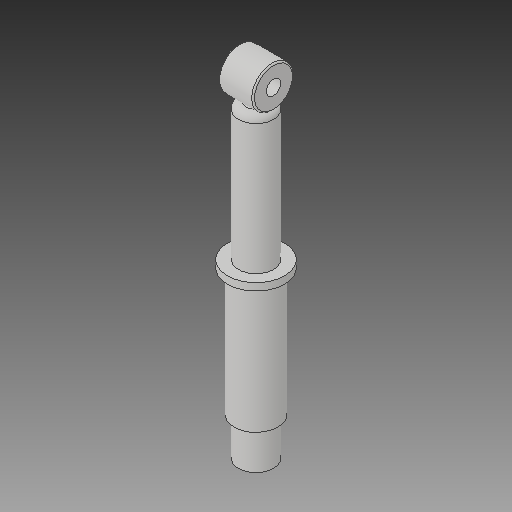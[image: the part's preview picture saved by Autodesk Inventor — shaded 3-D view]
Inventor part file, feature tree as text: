
AUTODESK INVENTOR PART (.ipt)
format: ipt  version: 2018 (Build 220112000, 112)  size: 138,752 bytes
history: native  units: mm
features: sketch x7, extrude x5, fillet x3, hole x2, other x1
ambient origin geometry x8: Origin, YZ Plane, XZ Plane, XY Plane, X Axis, Y Axis, Z Axis, Center Point
bodies: Body1 (feature_tree)
feature tree (18):
  other  "ソリッド1"
  extrude  "押し出し1"  Depth=24.0mm
  extrude  "押し出し2"  Depth=94.0mm TaperAngle=0.0deg
  hole  "穴1"  [1 undecoded]
  fillet  "フィレット2"  Radius=14.1mm
  fillet  "フィレット3"  Radius=24.0mm
  fillet  "フィレット4"  Radius=5.0mm
  extrude  "押し出し3"  Depth=1.0mm
  extrude  "押し出し4"  Depth=1.0mm
  extrude  "押し出し5"  Depth=39.0mm
  hole  "穴2"  [1 undecoded]
  sketch  "スケッチ1"
  sketch  "スケッチ3"
  sketch  "スケッチ4"
  sketch  "スケッチ5"
  sketch  "スケッチ6"
  sketch  "スケッチ7"
  sketch  "スケッチ8"
note: 2 required parameter values undecoded (feature->parameter linkage not recoverable at this tier; creation-order binding heuristic only, values carry confidence <= 0.55)
